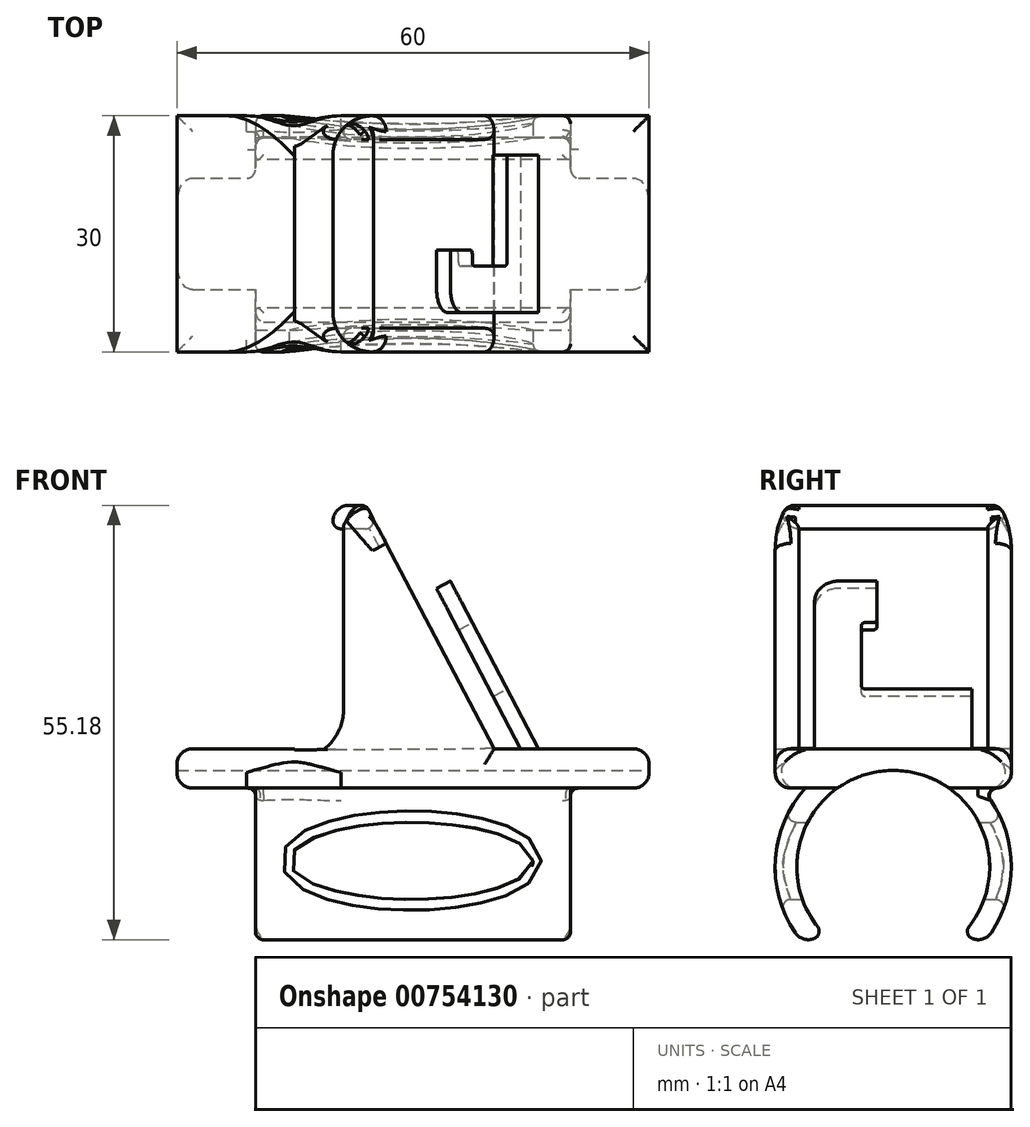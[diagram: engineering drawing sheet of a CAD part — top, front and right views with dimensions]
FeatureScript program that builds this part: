
annotation { "Feature Type Name" : "Feature", "Feature Type Description" : "" }
export const myFeature = defineFeature(function(context is Context, id is Id, definition is map)
    precondition{}
    {
        {
            var Q0;
            Q0=qCreatedBy(makeId("Right.planeOp"),FACE);
            var sketch = newSketch(context, id + "F0", { "sketchPlane" : qUnion([Q0])});
            skLineSegment(sketch, "E0.bottom", {"start": v(7.05, 0) * mm, "end": v(37.05, 0) * mm});
            skLineSegment(sketch, "E0.top", {"start": v(7.05, 5) * mm, "end": v(37.05, 5) * mm});
            skLineSegment(sketch, "E0.left", {"start": v(7.05, 0) * mm, "end": v(7.05, 5) * mm});
            skLineSegment(sketch, "E0.right", {"start": v(37.05, 0) * mm, "end": v(37.05, 5) * mm});
            skSolve(sketch);
        }
        {
            var Q0;
            Q0=makeQuery(id+"F0.imprint","IMPRINT",FACE,{"disambiguationData":[TD([[makeQuery(id+"F0.imprint","IMPRINT",EDGE,{"derivedFrom":sQuery(id+"F0.wireOp",EDGE,"E0.bottom")}),1.0]])]});
            var sketch = newSketch(context, id + "F1", { "sketchPlane" : qUnion([Q0])});
            skCircle(sketch, "E1", {"center": v(22.05, -10) * mm, "radius": 15 * mm});
            skSolve(sketch);
        }
        {
            var Q0;
            Q0=makeQuery(id+"F0.imprint","IMPRINT",FACE,{"disambiguationData":[TD([[makeQuery(id+"F0.imprint","IMPRINT",EDGE,{"derivedFrom":sQuery(id+"F0.wireOp",EDGE,"E0.bottom")}),1.0]])]});
            extrude(context, id + "F2", {"entities" : qUnion([Q0]), "oppositeDirection" : true, "depth" : 60 * mm, "offsetDistance" : 25 * mm});
        }
        {
            var Q0;
            {var subQ0=sQuery(id+"F1.wireOp",EDGE,"E1");var subQ1=makeQuery(id+"F0.imprint","IMPRINT",EDGE,{"derivedFrom":sQuery(id+"F0.wireOp",EDGE,"E0.bottom")});var subQ2=makeQuery(id+"F1.imprint","INTERSECT",VERTEX,{"disambiguationData":[OD(0.0)],"derivedFrom":[subQ1,subQ0]});Q0=makeQuery(id+"F1.imprint","IMPRINT",FACE,{"disambiguationData":[TD([[makeQuery(id+"F1.imprint","IMPRINT",EDGE,{"disambiguationData":[TD([[subQ2,1.0]])],"derivedFrom":subQ0}),1.0]])]});}
            extrude(context, id + "F3", {"entities" : qUnion([Q0]), "operationType" : NewBodyOperationType.ADD, "oppositeDirection" : true, "depth" : 50 * mm, "offsetDistance" : 25 * mm, "hasSecondDirection" : true, "secondDirectionOppositeDirection" : true, "secondDirectionDepth" : 10 * mm});
        }
        {
            var Q0;
            Q0=makeQuery(id+"F3.opExtrude","CAP_FACE",FACE,{"disambiguationData":[OSD([sQuery(id+"F0.wireOp",EDGE,"E0.bottom"),sQuery(id+"F1.wireOp",EDGE,"E1")])],"isStart":true});
            var sketch = newSketch(context, id + "F4", { "sketchPlane" : qUnion([Q0])});
            skCircle(sketch, "E2", {"center": v(22.05, -10) * mm, "radius": 12.25 * mm});
            skSolve(sketch);
        }
        {
            var Q0;
            Q0 = qSketchRegion(id + "F4", true);
            extrude(context, id + "F5", {"entities" : qUnion([Q0]), "operationType" : NewBodyOperationType.REMOVE, "oppositeDirection" : true, "depth" : 50 * mm, "offsetDistance" : 25 * mm, "hasSecondDirection" : true, "secondDirectionOppositeDirection" : false, "secondDirectionDepth" : 10 * mm});
        }
        {
            var Q0;
            Q0=makeQuery(id+"F2.opExtrude","CAP_FACE",FACE,{"disambiguationData":[OSD([sQuery(id+"F0.wireOp",EDGE,"E0.bottom"),sQuery(id+"F0.wireOp",EDGE,"E0.top"),sQuery(id+"F0.wireOp",EDGE,"E0.left"),sQuery(id+"F0.wireOp",EDGE,"E0.right")])],"isStart":true});
            var sketch = newSketch(context, id + "F6", { "sketchPlane" : qUnion([Q0])});
            skLineSegment(sketch, "E3.bottom", {"start": v(31.1, -25.8) * mm, "end": v(13, -25.8) * mm});
            skLineSegment(sketch, "E3.top", {"start": v(31.1, -13.27) * mm, "end": v(13, -13.27) * mm});
            skLineSegment(sketch, "E3.left", {"start": v(31.1, -25.8) * mm, "end": v(31.1, -13.27) * mm});
            skLineSegment(sketch, "E3.right", {"start": v(13, -25.8) * mm, "end": v(13, -13.27) * mm});
            skPoint(sketch, "E3.middle", {"position": v(22.05, -19.53) * mm});
            skPoint(sketch, "E3.middle.positionSnap0", {"position": v(22.05, 2.25) * mm});
            skPoint(sketch, "E3.centerSnap0", {"position": v(22.05, 2.25) * mm});
            skSolve(sketch);
        }
        {
            var Q0;
            Q0 = qSketchRegion(id + "F6", true);
            extrude(context, id + "F7", {"entities" : qUnion([Q0]), "operationType" : NewBodyOperationType.REMOVE, "oppositeDirection" : true, "depth" : 50 * mm, "offsetDistance" : 25 * mm});
        }
        {
            var Q0;
            Q0=makeQuery(id+"F2.opExtrude","SWEPT_FACE",FACE,{"disambiguationData":[OSD([sQuery(id+"F0.wireOp",EDGE,"E0.left")])]});
            var sketch = newSketch(context, id + "F8", { "sketchPlane" : qUnion([Q0])});
            skLineSegment(sketch, "E4", {"start": v(-16.32, 5) * mm, "end": v(-27, 25.37) * mm});
            skLineSegment(sketch, "E5", {"start": v(-27, 25.37) * mm, "end": v(-25.24, 26.3) * mm});
            skLineSegment(sketch, "E6", {"start": v(-25.24, 26.3) * mm, "end": v(-14.06, 5) * mm});
            skLineSegment(sketch, "E7", {"start": v(-14.06, 5) * mm, "end": v(-16.32, 5) * mm});
            skLineSegment(sketch, "E8", {"start": v(-19.7, 5) * mm, "end": v(-35.94, 35.92) * mm});
            skLineSegment(sketch, "E9", {"start": v(-35.94, 35.92) * mm, "end": v(-40.17, 35.92) * mm});
            skLineSegment(sketch, "E10", {"start": v(-40.17, 35.92) * mm, "end": v(-40.17, 5) * mm});
            skLineSegment(sketch, "E11", {"start": v(-40.17, 5) * mm, "end": v(-19.7, 5) * mm});
            skSolve(sketch);
        }
        {
            var Q0;
            Q0=makeQuery(id+"F8.imprint","IMPRINT",FACE,{"disambiguationData":[TD([[makeQuery(id+"F8.imprint","IMPRINT",EDGE,{"derivedFrom":sQuery(id+"F8.wireOp",EDGE,"E4")}),-1.0]])]});
            extrude(context, id + "F9", {"entities" : qUnion([Q0]), "operationType" : NewBodyOperationType.ADD, "oppositeDirection" : true, "depth" : 25 * mm, "offsetDistance" : 25 * mm, "hasSecondDirection" : true, "secondDirectionOppositeDirection" : true, "secondDirectionDepth" : 5 * mm});
        }
        {
            var Q0;
            Q0=makeQuery(id+"F8.imprint","IMPRINT",FACE,{"disambiguationData":[TD([[makeQuery(id+"F8.imprint","IMPRINT",EDGE,{"derivedFrom":sQuery(id+"F8.wireOp",EDGE,"E8")}),1.0]])]});
            extrude(context, id + "F10", {"entities" : qUnion([Q0]), "operationType" : NewBodyOperationType.ADD, "oppositeDirection" : true, "depth" : 30 * mm, "offsetDistance" : 25 * mm});
        }
        {
            var Q0;
            Q0=makeQuery(id+"F9.opExtrude","SWEPT_FACE",FACE,{"disambiguationData":[OSD([sQuery(id+"F8.wireOp",EDGE,"E6")])]});
            var sketch = newSketch(context, id + "F11", { "sketchPlane" : qUnion([Q0])});
            skLineSegment(sketch, "E12", {"start": v(32.05, 35.01) * mm, "end": v(32.05, 19.55) * mm});
            skLineSegment(sketch, "E13", {"start": v(32.05, 19.55) * mm, "end": v(17.98, 19.55) * mm});
            skLineSegment(sketch, "E14", {"start": v(17.98, 19.55) * mm, "end": v(17.98, 29.07) * mm});
            skLineSegment(sketch, "E15", {"start": v(17.98, 29.07) * mm, "end": v(20, 29.07) * mm});
            skLineSegment(sketch, "E16", {"start": v(20, 29.07) * mm, "end": v(20, 35.01) * mm});
            skLineSegment(sketch, "E17", {"start": v(20, 35.01) * mm, "end": v(32.05, 35.01) * mm});
            skSolve(sketch);
        }
        {
            var Q0;
            Q0 = qSketchRegion(id + "F11", true);
            extrude(context, id + "F12", {"entities" : qUnion([Q0]), "operationType" : NewBodyOperationType.REMOVE, "oppositeDirection" : true, "depth" : 2 * mm, "offsetDistance" : 25 * mm});
        }
        {
            var Q0;
            Q0=makeQuery(id+"F12.boolean.opBoolean","COPY",EDGE,{"derivedFrom":makeQuery(id+"F12.opExtrude","SWEPT_EDGE",EDGE,{"disambiguationData":[OSD([sQuery(id+"F8.wireOp",EDGE,"E5"),sQuery(id+"F8.wireOp",EDGE,"E6"),sQuery(id+"F11.wireOp",EDGE,"E16"),sQuery(id+"F11.wireOp",EDGE,"E17")])]})});
            var Q1;
            Q1=makeQuery(id+"F9.opExtrude","CAP_EDGE",EDGE,{"disambiguationData":[OSD([sQuery(id+"F8.wireOp",EDGE,"E5")])],"isStart":true});
            fillet(context, id + "F13", {"entities" : qUnion([Q0, Q1]), "radius" : 3 * mm, "tangentPropagation" : true, "allowEdgeOverflow" : false});
        }
        {
            var Q0;
            Q0=makeQuery(id+"F12.boolean.opBoolean","COPY",EDGE,{"derivedFrom":makeQuery(id+"F12.opExtrude","SWEPT_EDGE",EDGE,{"disambiguationData":[OSD([sQuery(id+"F8.wireOp",EDGE,"E6"),sQuery(id+"F11.wireOp",EDGE,"E12"),sQuery(id+"F11.wireOp",EDGE,"E13")])]})});
            var Q1;
            Q1=makeQuery(id+"F12.boolean.opBoolean","COPY",EDGE,{"derivedFrom":makeQuery(id+"F12.opExtrude","SWEPT_EDGE",EDGE,{"disambiguationData":[OSD([sQuery(id+"F11.wireOp",EDGE,"E15"),sQuery(id+"F11.wireOp",EDGE,"E16")])]})});
            var Q2;
            Q2=makeQuery(id+"F12.boolean.opBoolean","COPY",EDGE,{"derivedFrom":makeQuery(id+"F12.opExtrude","SWEPT_EDGE",EDGE,{"disambiguationData":[OSD([sQuery(id+"F11.wireOp",EDGE,"E14"),sQuery(id+"F11.wireOp",EDGE,"E15")])]})});
            var Q3;
            Q3=makeQuery(id+"F12.boolean.opBoolean","COPY",EDGE,{"derivedFrom":makeQuery(id+"F12.opExtrude","SWEPT_EDGE",EDGE,{"disambiguationData":[OSD([sQuery(id+"F11.wireOp",EDGE,"E13"),sQuery(id+"F11.wireOp",EDGE,"E14")])]})});
            fillet(context, id + "F14", {"entities" : qUnion([Q0, Q1, Q2, Q3]), "radius" : 0.5 * mm, "tangentPropagation" : true, "allowEdgeOverflow" : false});
        }
        {
            var Q0;
            Q0=makeQuery(id+"F10.opExtrude","CAP_EDGE",EDGE,{"disambiguationData":[OSD([sQuery(id+"F8.wireOp",EDGE,"E10")])],"isStart":false});
            var Q1;
            Q1=makeQuery(id+"F10.opExtrude","CAP_EDGE",EDGE,{"disambiguationData":[OSD([sQuery(id+"F8.wireOp",EDGE,"E10")])],"isStart":true});
            var Q2;
            Q2=makeQuery(id+"F10.opExtrude","SWEPT_EDGE",EDGE,{"disambiguationData":[OSD([sQuery(id+"F0.wireOp",EDGE,"E0.top"),sQuery(id+"F0.wireOp",EDGE,"E0.left"),sQuery(id+"F8.wireOp",EDGE,"E10"),sQuery(id+"F8.wireOp",EDGE,"E11")])]});
            fillet(context, id + "F15", {"entities" : qUnion([Q0, Q1, Q2]), "radius" : 5 * mm, "tangentPropagation" : true, "allowEdgeOverflow" : false});
        }
        {
            var Q0;
            Q0=makeQuery(id+"F10.opExtrude","SWEPT_EDGE",EDGE,{"disambiguationData":[OSD([sQuery(id+"F8.wireOp",EDGE,"E9"),sQuery(id+"F8.wireOp",EDGE,"E10")])]});
            var Q1;
            Q1=makeQuery(id+"F10.opExtrude","CAP_EDGE",EDGE,{"disambiguationData":[OSD([sQuery(id+"F8.wireOp",EDGE,"E8")])],"isStart":true});
            var Q2;
            Q2=makeQuery(id+"F10.opExtrude","CAP_EDGE",EDGE,{"disambiguationData":[OSD([sQuery(id+"F8.wireOp",EDGE,"E8")])],"isStart":false});
            var Q3;
            Q3=makeQuery(id+"F2.opExtrude","CAP_EDGE",EDGE,{"disambiguationData":[OSD([sQuery(id+"F0.wireOp",EDGE,"E0.top")])],"isStart":false});
            var Q4;
            {var subQ0=sQuery(id+"F8.wireOp",EDGE,"E8");var subQ1=sQuery(id+"F0.wireOp",EDGE,"E0.right");var subQ2=sQuery(id+"F0.wireOp",EDGE,"E0.top");Q4=makeQuery(id+"F10.boolean.opBoolean","SPLIT",EDGE,{"disambiguationData":[TD([makeQuery(id+"F10.opExtrude","SWEPT_FACE",FACE,{"disambiguationData":[OSD([subQ0])]})])],"derivedFrom":makeQuery(id+"F2.opExtrude","SWEPT_EDGE",EDGE,{"disambiguationData":[OSD([subQ2,subQ1])]})});}
            var Q5;
            Q5=makeQuery(id+"F2.opExtrude","CAP_EDGE",EDGE,{"disambiguationData":[OSD([sQuery(id+"F0.wireOp",EDGE,"E0.top")])],"isStart":true});
            var Q6;
            {var subQ0=sQuery(id+"F8.wireOp",EDGE,"E8");var subQ1=sQuery(id+"F0.wireOp",EDGE,"E0.left");var subQ2=sQuery(id+"F0.wireOp",EDGE,"E0.top");Q6=makeQuery(id+"F10.boolean.opBoolean","SPLIT",EDGE,{"disambiguationData":[TD([makeQuery(id+"F10.opExtrude","SWEPT_FACE",FACE,{"disambiguationData":[OSD([subQ0])]})])],"derivedFrom":makeQuery(id+"F2.opExtrude","SWEPT_EDGE",EDGE,{"disambiguationData":[OSD([subQ2,subQ1])]})});}
            var Q7;
            {var subQ0=sQuery(id+"F0.wireOp",EDGE,"E0.bottom");var subQ1=sQuery(id+"F0.wireOp",EDGE,"E0.left");Q7=makeQuery(id+"F5.boolean.opBoolean","SPLIT",EDGE,{"disambiguationData":[TD([makeQuery(id+"F2.opExtrude","SWEPT_FACE",FACE,{"disambiguationData":[OSD([subQ1])]})])],"derivedFrom":makeQuery(id+"F2.opExtrude","CAP_EDGE",EDGE,{"disambiguationData":[OSD([subQ0])],"isStart":false})});}
            var Q8;
            {var subQ0=sQuery(id+"F0.wireOp",EDGE,"E0.bottom");var subQ1=sQuery(id+"F0.wireOp",EDGE,"E0.right");Q8=makeQuery(id+"F5.boolean.opBoolean","SPLIT",EDGE,{"disambiguationData":[TD([makeQuery(id+"F2.opExtrude","SWEPT_FACE",FACE,{"disambiguationData":[OSD([subQ1])]})])],"derivedFrom":makeQuery(id+"F2.opExtrude","CAP_EDGE",EDGE,{"disambiguationData":[OSD([subQ0])],"isStart":false})});}
            var Q9;
            Q9=makeQuery(id+"F2.opExtrude","SWEPT_EDGE",EDGE,{"disambiguationData":[OSD([sQuery(id+"F0.wireOp",EDGE,"E0.bottom"),sQuery(id+"F0.wireOp",EDGE,"E0.right")])]});
            var Q10;
            Q10=makeQuery(id+"F2.opExtrude","SWEPT_EDGE",EDGE,{"disambiguationData":[OSD([sQuery(id+"F0.wireOp",EDGE,"E0.bottom"),sQuery(id+"F0.wireOp",EDGE,"E0.left")])]});
            var Q11;
            {var subQ0=sQuery(id+"F0.wireOp",EDGE,"E0.bottom");var subQ1=sQuery(id+"F0.wireOp",EDGE,"E0.left");Q11=makeQuery(id+"F5.boolean.opBoolean","SPLIT",EDGE,{"disambiguationData":[TD([makeQuery(id+"F2.opExtrude","SWEPT_FACE",FACE,{"disambiguationData":[OSD([subQ1])]})])],"derivedFrom":makeQuery(id+"F2.opExtrude","CAP_EDGE",EDGE,{"disambiguationData":[OSD([subQ0])],"isStart":true})});}
            var Q12;
            {var subQ0=sQuery(id+"F0.wireOp",EDGE,"E0.bottom");var subQ1=sQuery(id+"F0.wireOp",EDGE,"E0.right");Q12=makeQuery(id+"F5.boolean.opBoolean","SPLIT",EDGE,{"disambiguationData":[TD([makeQuery(id+"F2.opExtrude","SWEPT_FACE",FACE,{"disambiguationData":[OSD([subQ1])]})])],"derivedFrom":makeQuery(id+"F2.opExtrude","CAP_EDGE",EDGE,{"disambiguationData":[OSD([subQ0])],"isStart":true})});}
            fillet(context, id + "F16", {"entities" : qUnion([Q0, Q1, Q2, Q3, Q4, Q5, Q6, Q7, Q8, Q9, Q10, Q11, Q12]), "radius" : 2 * mm, "tangentPropagation" : true, "allowEdgeOverflow" : false});
        }
        {
            var Q0;
            Q0=makeQuery(id+"F10.boolean.opBoolean","MERGE",FACE,{"derivedFrom":[makeQuery(id+"F2.opExtrude","SWEPT_FACE",FACE,{"disambiguationData":[OSD([sQuery(id+"F0.wireOp",EDGE,"E0.left")])]}),makeQuery(id+"F10.opExtrude","CAP_FACE",FACE,{"disambiguationData":[OSD([sQuery(id+"F8.wireOp",EDGE,"E8"),sQuery(id+"F8.wireOp",EDGE,"E9"),sQuery(id+"F8.wireOp",EDGE,"E10"),sQuery(id+"F8.wireOp",EDGE,"E11")])],"isStart":true})]});
            var sketch = newSketch(context, id + "F17", { "sketchPlane" : qUnion([Q0])});
            skLineSegment(sketch, "E18", {"start": v(-19.51, 5.04) * mm, "end": v(-34.16, 32.95) * mm});
            skLineSegment(sketch, "E19", {"start": v(-34.16, 32.95) * mm, "end": v(-45.06, 32.95) * mm});
            skLineSegment(sketch, "E20", {"start": v(-45.06, 32.95) * mm, "end": v(-45.06, 4.87) * mm});
            skLineSegment(sketch, "E21", {"start": v(-45.06, 4.87) * mm, "end": v(-19.51, 5.04) * mm});
            skSolve(sketch);
        }
        {
            var Q0;
            Q0 = qSketchRegion(id + "F17", true);
            extrude(context, id + "F18", {"entities" : qUnion([Q0]), "operationType" : NewBodyOperationType.REMOVE, "oppositeDirection" : true, "depth" : 27 * mm, "offsetDistance" : 25 * mm, "hasSecondDirection" : true, "secondDirectionOppositeDirection" : true, "secondDirectionDepth" : 3 * mm});
        }
        {
            var Q0;
            {var subQ0=sQuery(id+"F8.wireOp",EDGE,"E10");Q0=makeQuery(id+"F18.boolean.opBoolean","INTERSECT",EDGE,{"derivedFrom":[makeQuery(id+"F15.opFillet","BLEND_FACE",FACE,{"disambiguationData":[OSD([subQ0]),TDD([makeQuery(id+"F10.opExtrude","CAP_EDGE",EDGE,{"disambiguationData":[OSD([subQ0])],"isStart":true})])]}),makeQuery(id+"F18.opExtrude","CAP_FACE",FACE,{"disambiguationData":[OSD([sQuery(id+"F17.wireOp",EDGE,"E18"),sQuery(id+"F17.wireOp",EDGE,"E19"),sQuery(id+"F17.wireOp",EDGE,"E20"),sQuery(id+"F17.wireOp",EDGE,"E21")])],"isStart":true})]});}
            var Q1;
            Q1=makeQuery(id+"F18.boolean.opBoolean","INTERSECT",EDGE,{"derivedFrom":[makeQuery(id+"F10.opExtrude","SWEPT_FACE",FACE,{"disambiguationData":[OSD([sQuery(id+"F8.wireOp",EDGE,"E10")])]}),makeQuery(id+"F18.opExtrude","SWEPT_FACE",FACE,{"disambiguationData":[OSD([sQuery(id+"F17.wireOp",EDGE,"E19")])]})]});
            var Q2;
            {var subQ0=sQuery(id+"F8.wireOp",EDGE,"E10");Q2=makeQuery(id+"F18.boolean.opBoolean","INTERSECT",EDGE,{"derivedFrom":[makeQuery(id+"F15.opFillet","BLEND_FACE",FACE,{"disambiguationData":[OSD([subQ0]),TDD([makeQuery(id+"F10.opExtrude","CAP_EDGE",EDGE,{"disambiguationData":[OSD([subQ0])],"isStart":false})])]}),makeQuery(id+"F18.opExtrude","CAP_FACE",FACE,{"disambiguationData":[OSD([sQuery(id+"F17.wireOp",EDGE,"E18"),sQuery(id+"F17.wireOp",EDGE,"E19"),sQuery(id+"F17.wireOp",EDGE,"E20"),sQuery(id+"F17.wireOp",EDGE,"E21")])],"isStart":false})]});}
            var Q3;
            {var subQ0=sQuery(id+"F8.wireOp",EDGE,"E11");var subQ1=sQuery(id+"F8.wireOp",EDGE,"E10");var subQ2=sQuery(id+"F0.wireOp",EDGE,"E0.left");var subQ3=sQuery(id+"F0.wireOp",EDGE,"E0.top");Q3=makeQuery(id+"F18.boolean.opBoolean","INTERSECT",EDGE,{"derivedFrom":[makeQuery(id+"F15.opFillet","BLEND_FACE",FACE,{"disambiguationData":[OSD([subQ3,subQ2,subQ1,subQ0]),TDD([makeQuery(id+"F10.opExtrude","CAP_VERTEX",VERTEX,{"disambiguationData":[OSD([subQ3,subQ2,subQ1,subQ0])],"isStart":true})])]}),makeQuery(id+"F18.opExtrude","SWEPT_FACE",FACE,{"disambiguationData":[OSD([sQuery(id+"F17.wireOp",EDGE,"E21")])]})]});}
            var Q4;
            {var subQ0=sQuery(id+"F8.wireOp",EDGE,"E11");var subQ1=sQuery(id+"F8.wireOp",EDGE,"E10");var subQ2=sQuery(id+"F0.wireOp",EDGE,"E0.left");var subQ3=sQuery(id+"F0.wireOp",EDGE,"E0.top");Q4=makeQuery(id+"F18.boolean.opBoolean","INTERSECT",EDGE,{"derivedFrom":[makeQuery(id+"F15.opFillet","BLEND_FACE",FACE,{"disambiguationData":[OSD([subQ3,subQ2,subQ1,subQ0]),TDD([makeQuery(id+"F10.opExtrude","CAP_VERTEX",VERTEX,{"disambiguationData":[OSD([subQ3,subQ2,subQ1,subQ0])],"isStart":false})])]}),makeQuery(id+"F18.opExtrude","SWEPT_FACE",FACE,{"disambiguationData":[OSD([sQuery(id+"F17.wireOp",EDGE,"E21")])]})]});}
            var Q5;
            Q5=makeQuery(id+"F18.boolean.opBoolean","INTERSECT",EDGE,{"derivedFrom":[makeQuery(id+"F10.opExtrude","SWEPT_FACE",FACE,{"disambiguationData":[OSD([sQuery(id+"F8.wireOp",EDGE,"E8")])]}),makeQuery(id+"F18.opExtrude","CAP_FACE",FACE,{"disambiguationData":[OSD([sQuery(id+"F17.wireOp",EDGE,"E18"),sQuery(id+"F17.wireOp",EDGE,"E19"),sQuery(id+"F17.wireOp",EDGE,"E20"),sQuery(id+"F17.wireOp",EDGE,"E21")])],"isStart":true})]});
            var Q6;
            Q6=makeQuery(id+"F18.boolean.opBoolean","INTERSECT",EDGE,{"derivedFrom":[makeQuery(id+"F10.opExtrude","SWEPT_FACE",FACE,{"disambiguationData":[OSD([sQuery(id+"F8.wireOp",EDGE,"E8")])]}),makeQuery(id+"F18.opExtrude","CAP_FACE",FACE,{"disambiguationData":[OSD([sQuery(id+"F17.wireOp",EDGE,"E18"),sQuery(id+"F17.wireOp",EDGE,"E19"),sQuery(id+"F17.wireOp",EDGE,"E20"),sQuery(id+"F17.wireOp",EDGE,"E21")])],"isStart":false})]});
            fillet(context, id + "F19", {"entities" : qUnion([Q0, Q1, Q2, Q3, Q4, Q5, Q6]), "radius" : 1 * mm, "tangentPropagation" : true, "allowEdgeOverflow" : false});
        }
        {
            var Q0;
            Q0=makeQuery(id+"F18.boolean.opBoolean","INTERSECT",EDGE,{"derivedFrom":[makeQuery(id+"F10.opExtrude","SWEPT_FACE",FACE,{"disambiguationData":[OSD([sQuery(id+"F8.wireOp",EDGE,"E8")])]}),makeQuery(id+"F18.opExtrude","SWEPT_FACE",FACE,{"disambiguationData":[OSD([sQuery(id+"F17.wireOp",EDGE,"E19")])]})]});
            var Q1;
            Q1=makeQuery(id+"F10.opExtrude","SWEPT_EDGE",EDGE,{"disambiguationData":[OSD([sQuery(id+"F8.wireOp",EDGE,"E8"),sQuery(id+"F8.wireOp",EDGE,"E9")])]});
            fillet(context, id + "F20", {"entities" : qUnion([Q0, Q1]), "radius" : 1 * mm, "tangentPropagation" : true, "allowEdgeOverflow" : false});
        }
        {
            var Q0;
            Q0=makeQuery(id+"F7.boolean.opBoolean","INTERSECT",EDGE,{"derivedFrom":[makeQuery(id+"F3.opExtrude","SWEPT_FACE",FACE,{"disambiguationData":[OSD([sQuery(id+"F1.wireOp",EDGE,"E1")])]}),makeQuery(id+"F7.opExtrude","SWEPT_FACE",FACE,{"disambiguationData":[OSD([sQuery(id+"F6.wireOp",EDGE,"E3.right")])]})]});
            var Q1;
            Q1=makeQuery(id+"F7.boolean.opBoolean","INTERSECT",EDGE,{"derivedFrom":[makeQuery(id+"F3.opExtrude","SWEPT_FACE",FACE,{"disambiguationData":[OSD([sQuery(id+"F1.wireOp",EDGE,"E1")])]}),makeQuery(id+"F7.opExtrude","SWEPT_FACE",FACE,{"disambiguationData":[OSD([sQuery(id+"F6.wireOp",EDGE,"E3.left")])]})]});
            fillet(context, id + "F21", {"entities" : qUnion([Q0, Q1]), "radius" : 2 * mm, "tangentPropagation" : true, "allowEdgeOverflow" : false});
        }
        {
            var Q0;
            Q0=makeQuery(id+"F21.opFillet","BLEND_EDGE",EDGE,{"blendedFrom":[makeQuery(id+"F7.boolean.opBoolean","INTERSECT",EDGE,{"derivedFrom":[makeQuery(id+"F3.opExtrude","SWEPT_FACE",FACE,{"disambiguationData":[OSD([sQuery(id+"F1.wireOp",EDGE,"E1")])]}),makeQuery(id+"F7.opExtrude","SWEPT_FACE",FACE,{"disambiguationData":[OSD([sQuery(id+"F6.wireOp",EDGE,"E3.right")])]})]}),makeQuery(id+"F5.boolean.opBoolean","COPY",FACE,{"derivedFrom":makeQuery(id+"F5.opExtrude","SWEPT_FACE",FACE,{"disambiguationData":[OSD([sQuery(id+"F4.wireOp",EDGE,"E2")])]})})],"blendedInto":[makeQuery(id+"F5.boolean.opBoolean","COPY",FACE,{"derivedFrom":makeQuery(id+"F5.opExtrude","SWEPT_FACE",FACE,{"disambiguationData":[OSD([sQuery(id+"F4.wireOp",EDGE,"E2")])]})})]});
            var Q1;
            Q1=makeQuery(id+"F21.opFillet","BLEND_EDGE",EDGE,{"blendedFrom":[makeQuery(id+"F7.boolean.opBoolean","INTERSECT",EDGE,{"derivedFrom":[makeQuery(id+"F3.opExtrude","SWEPT_FACE",FACE,{"disambiguationData":[OSD([sQuery(id+"F1.wireOp",EDGE,"E1")])]}),makeQuery(id+"F7.opExtrude","SWEPT_FACE",FACE,{"disambiguationData":[OSD([sQuery(id+"F6.wireOp",EDGE,"E3.left")])]})]}),makeQuery(id+"F5.boolean.opBoolean","COPY",FACE,{"derivedFrom":makeQuery(id+"F5.opExtrude","SWEPT_FACE",FACE,{"disambiguationData":[OSD([sQuery(id+"F4.wireOp",EDGE,"E2")])]})})],"blendedInto":[makeQuery(id+"F5.boolean.opBoolean","COPY",FACE,{"derivedFrom":makeQuery(id+"F5.opExtrude","SWEPT_FACE",FACE,{"disambiguationData":[OSD([sQuery(id+"F4.wireOp",EDGE,"E2")])]})})]});
            var Q2;
            {var subQ1=sQuery(id+"F1.wireOp",EDGE,"E1");Q2=makeQuery(id+"F7.boolean.opBoolean","SPLIT",EDGE,{"disambiguationData":[TD([makeQuery(id+"F7.opExtrude","SWEPT_FACE",FACE,{"disambiguationData":[OSD([sQuery(id+"F6.wireOp",EDGE,"E3.left")])]})])],"derivedFrom":makeQuery(id+"F3.opExtrude","CAP_EDGE",EDGE,{"disambiguationData":[OSD([subQ1])],"isStart":true})});}
            var Q3;
            {var subQ1=sQuery(id+"F1.wireOp",EDGE,"E1");Q3=makeQuery(id+"F7.boolean.opBoolean","SPLIT",EDGE,{"disambiguationData":[TD([makeQuery(id+"F7.opExtrude","SWEPT_FACE",FACE,{"disambiguationData":[OSD([sQuery(id+"F6.wireOp",EDGE,"E3.right")])]})])],"derivedFrom":makeQuery(id+"F3.opExtrude","CAP_EDGE",EDGE,{"disambiguationData":[OSD([subQ1])],"isStart":true})});}
            var Q4;
            {var subQ1=sQuery(id+"F1.wireOp",EDGE,"E1");Q4=makeQuery(id+"F7.boolean.opBoolean","SPLIT",EDGE,{"disambiguationData":[TD([makeQuery(id+"F7.opExtrude","SWEPT_FACE",FACE,{"disambiguationData":[OSD([sQuery(id+"F6.wireOp",EDGE,"E3.right")])]})])],"derivedFrom":makeQuery(id+"F3.opExtrude","CAP_EDGE",EDGE,{"disambiguationData":[OSD([subQ1])],"isStart":false})});}
            var Q5;
            {var subQ1=sQuery(id+"F1.wireOp",EDGE,"E1");Q5=makeQuery(id+"F7.boolean.opBoolean","SPLIT",EDGE,{"disambiguationData":[TD([makeQuery(id+"F7.opExtrude","SWEPT_FACE",FACE,{"disambiguationData":[OSD([sQuery(id+"F6.wireOp",EDGE,"E3.left")])]})])],"derivedFrom":makeQuery(id+"F3.opExtrude","CAP_EDGE",EDGE,{"disambiguationData":[OSD([subQ1])],"isStart":false})});}
            fillet(context, id + "F22", {"entities" : qUnion([Q0, Q1, Q2, Q3, Q4, Q5]), "radius" : 1 * mm, "tangentPropagation" : true, "allowEdgeOverflow" : false});
        }
        {
            var Q0;
            Q0=makeQuery(id+"F10.boolean.opBoolean","MERGE",FACE,{"derivedFrom":[makeQuery(id+"F2.opExtrude","SWEPT_FACE",FACE,{"disambiguationData":[OSD([sQuery(id+"F0.wireOp",EDGE,"E0.left")])]}),makeQuery(id+"F10.opExtrude","CAP_FACE",FACE,{"disambiguationData":[OSD([sQuery(id+"F8.wireOp",EDGE,"E8"),sQuery(id+"F8.wireOp",EDGE,"E9"),sQuery(id+"F8.wireOp",EDGE,"E10"),sQuery(id+"F8.wireOp",EDGE,"E11")])],"isStart":true})]});
            var sketch = newSketch(context, id + "F23", { "sketchPlane" : qUnion([Q0])});
            skEllipse(sketch, "E22", {"center": v(-30.23, -9.24) * mm, "majorRadius": 15.48 * mm, "minorRadius": 4.9 * mm, "majorAxis": v(1, 0)});
            skSolve(sketch);
        }
        {
            var Q0;
            Q0=makeQuery(id+"F23.imprint","IMPRINT",FACE,{"disambiguationData":[TD([[makeQuery(id+"F23.imprint","IMPRINT",EDGE,{"derivedFrom":sQuery(id+"F23.wireOp",EDGE,"E22")}),1.0]])]});
            extrude(context, id + "F24", {"entities" : qUnion([Q0]), "operationType" : NewBodyOperationType.REMOVE, "oppositeDirection" : true, "depth" : 40 * mm, "offsetDistance" : 25 * mm});
        }
        {
            var Q0;
            {var subQ1=sQuery(id+"F1.wireOp",EDGE,"E1");Q0=makeQuery(id+"F24.boolean.opBoolean","INTERSECT",EDGE,{"derivedFrom":[makeQuery(id+"F7.boolean.opBoolean","SPLIT",FACE,{"disambiguationData":[TD([makeQuery(id+"F7.opExtrude","SWEPT_FACE",FACE,{"disambiguationData":[OSD([sQuery(id+"F6.wireOp",EDGE,"E3.right")])]})])],"derivedFrom":makeQuery(id+"F3.opExtrude","SWEPT_FACE",FACE,{"disambiguationData":[OSD([subQ1])]})}),makeQuery(id+"F24.opExtrude","SWEPT_FACE",FACE,{"disambiguationData":[OSD([sQuery(id+"F23.wireOp",EDGE,"E22")])]})]});}
            var Q1;
            {var subQ1=sQuery(id+"F1.wireOp",EDGE,"E1");Q1=makeQuery(id+"F7.boolean.opBoolean","SPLIT",FACE,{"disambiguationData":[TD([makeQuery(id+"F7.opExtrude","SWEPT_FACE",FACE,{"disambiguationData":[OSD([sQuery(id+"F6.wireOp",EDGE,"E3.left")])]})])],"derivedFrom":makeQuery(id+"F3.opExtrude","SWEPT_FACE",FACE,{"disambiguationData":[OSD([subQ1])]})});}
            fillet(context, id + "F25", {"entities" : qUnion([Q0, Q1]), "radius" : 1 * mm, "tangentPropagation" : true, "allowEdgeOverflow" : false});
        }
    });
